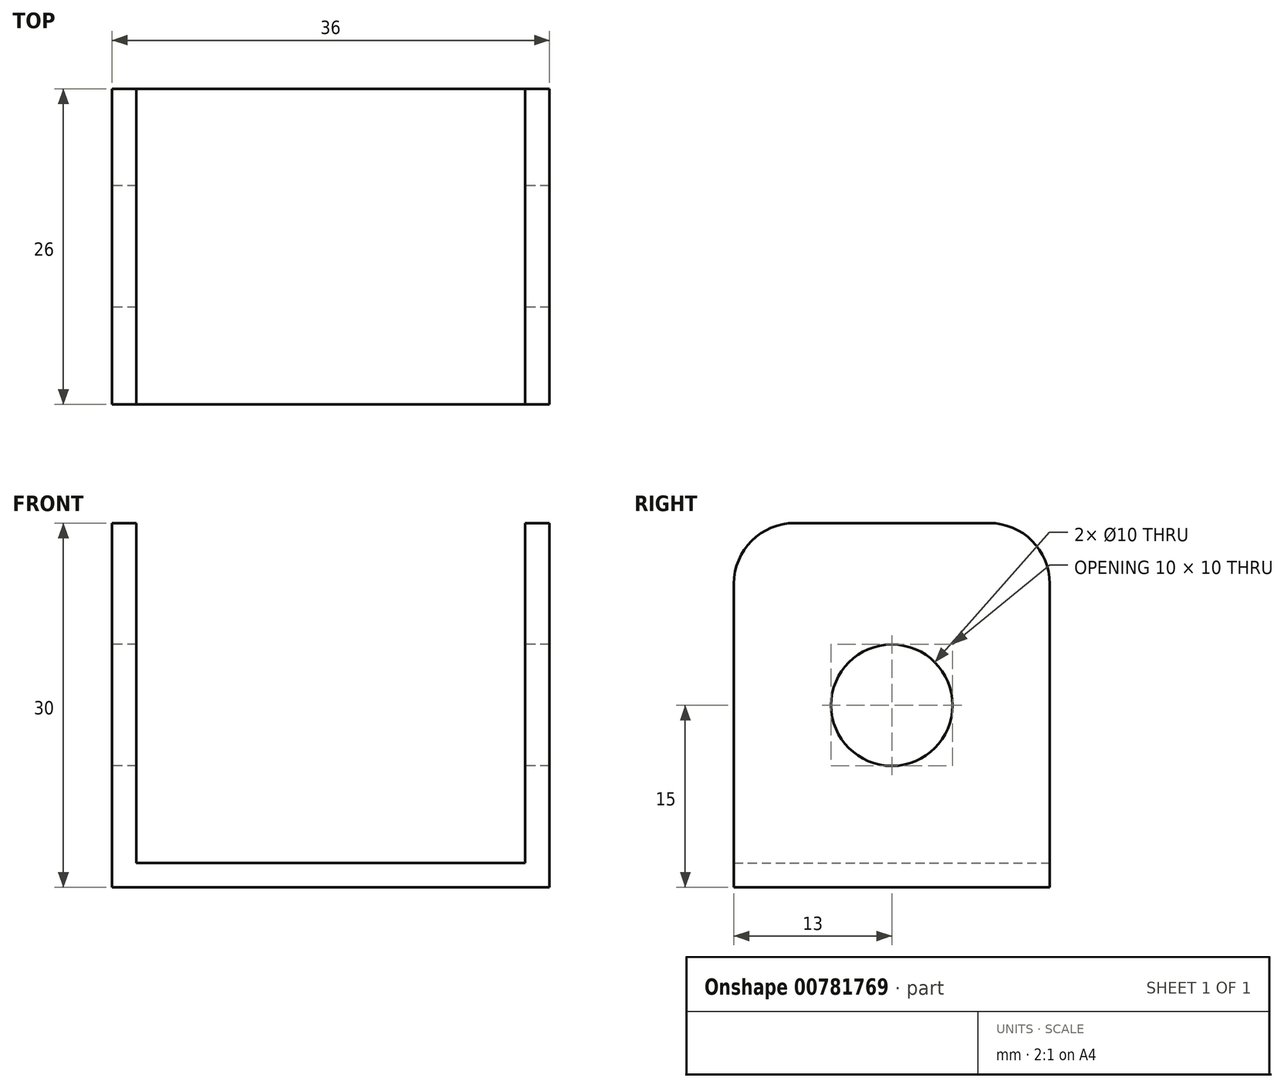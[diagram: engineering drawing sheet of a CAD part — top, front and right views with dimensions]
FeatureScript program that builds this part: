
annotation { "Feature Type Name" : "Feature", "Feature Type Description" : "" }
export const myFeature = defineFeature(function(context is Context, id is Id, definition is map)
    precondition{}
    {
        {
            var Q0;
            Q0=qCreatedBy(makeId("Front.planeOp"),FACE);
            var sketch = newSketch(context, id + "F0", { "sketchPlane" : qUnion([Q0])});
            skLineSegment(sketch, "E0.bottom", {"start": v(-18, 15) * mm, "end": v(-16, 15) * mm});
            skLineSegment(sketch, "E0.top", {"start": v(-18, -15) * mm, "end": v(18, -15) * mm});
            skLineSegment(sketch, "E0.left", {"start": v(-18, 15) * mm, "end": v(-18, -15) * mm});
            skLineSegment(sketch, "E0.right", {"start": v(18, 15) * mm, "end": v(18, -15) * mm});
            skPoint(sketch, "E0.middle", {"position": v(0, 0) * mm});
            skLineSegment(sketch, "E1", {"start": v(-16, 15) * mm, "end": v(-16, -13) * mm});
            skLineSegment(sketch, "E2", {"start": v(-16, -13) * mm, "end": v(16, -13) * mm});
            skLineSegment(sketch, "E3", {"start": v(16, -13) * mm, "end": v(16, 15) * mm});
            skLineSegment(sketch, "E4.trimOffspring", {"start": v(16, 15) * mm, "end": v(18, 15) * mm});
            skSolve(sketch);
        }
        {
            var Q0;
            Q0=makeQuery(id+"F0.imprint","IMPRINT",FACE,{"disambiguationData":[TD([[makeQuery(id+"F0.imprint","IMPRINT",EDGE,{"derivedFrom":sQuery(id+"F0.wireOp",EDGE,"E0.bottom")}),-1.0]])]});
            extrude(context, id + "F1", {"entities" : qUnion([Q0]), "depth" : 26 * mm, "offsetDistance" : 25 * mm});
        }
        {
            var Q0;
            Q0=makeQuery(id+"F1.opExtrude","CAP_EDGE",EDGE,{"disambiguationData":[OSD([sQuery(id+"F0.wireOp",EDGE,"E0.bottom")])],"isStart":true});
            var Q1;
            Q1=makeQuery(id+"F1.opExtrude","CAP_EDGE",EDGE,{"disambiguationData":[OSD([sQuery(id+"F0.wireOp",EDGE,"E4.trimOffspring")])],"isStart":true});
            var Q2;
            Q2=makeQuery(id+"F1.opExtrude","CAP_EDGE",EDGE,{"disambiguationData":[OSD([sQuery(id+"F0.wireOp",EDGE,"E0.bottom")])],"isStart":false});
            var Q3;
            Q3=makeQuery(id+"F1.opExtrude","CAP_EDGE",EDGE,{"disambiguationData":[OSD([sQuery(id+"F0.wireOp",EDGE,"E4.trimOffspring")])],"isStart":false});
            fillet(context, id + "F2", {"entities" : qUnion([Q0, Q1, Q2, Q3]), "radius" : 5 * mm, "tangentPropagation" : true, "allowEdgeOverflow" : false});
        }
        {
            var Q0;
            Q0=makeQuery(id+"F1.opExtrude","SWEPT_FACE",FACE,{"disambiguationData":[OSD([sQuery(id+"F0.wireOp",EDGE,"E0.left")])]});
            var sketch = newSketch(context, id + "F3", { "sketchPlane" : qUnion([Q0])});
            skCircle(sketch, "E5", {"center": v(13, 0) * mm, "radius": 5 * mm});
            skPoint(sketch, "E5.centerSnap0", {"position": v(13, 15) * mm});
            skSolve(sketch);
        }
        {
            var Q0;
            Q0=makeQuery(id+"F3.imprint","IMPRINT",FACE,{"disambiguationData":[TD([[makeQuery(id+"F3.imprint","IMPRINT",EDGE,{"derivedFrom":sQuery(id+"F3.wireOp",EDGE,"E5")}),1.0]])]});
            extrude(context, id + "F4", {"entities" : qUnion([Q0]), "operationType" : NewBodyOperationType.REMOVE, "oppositeDirection" : true, "depth" : 40 * mm, "offsetDistance" : 25 * mm});
        }
    });
